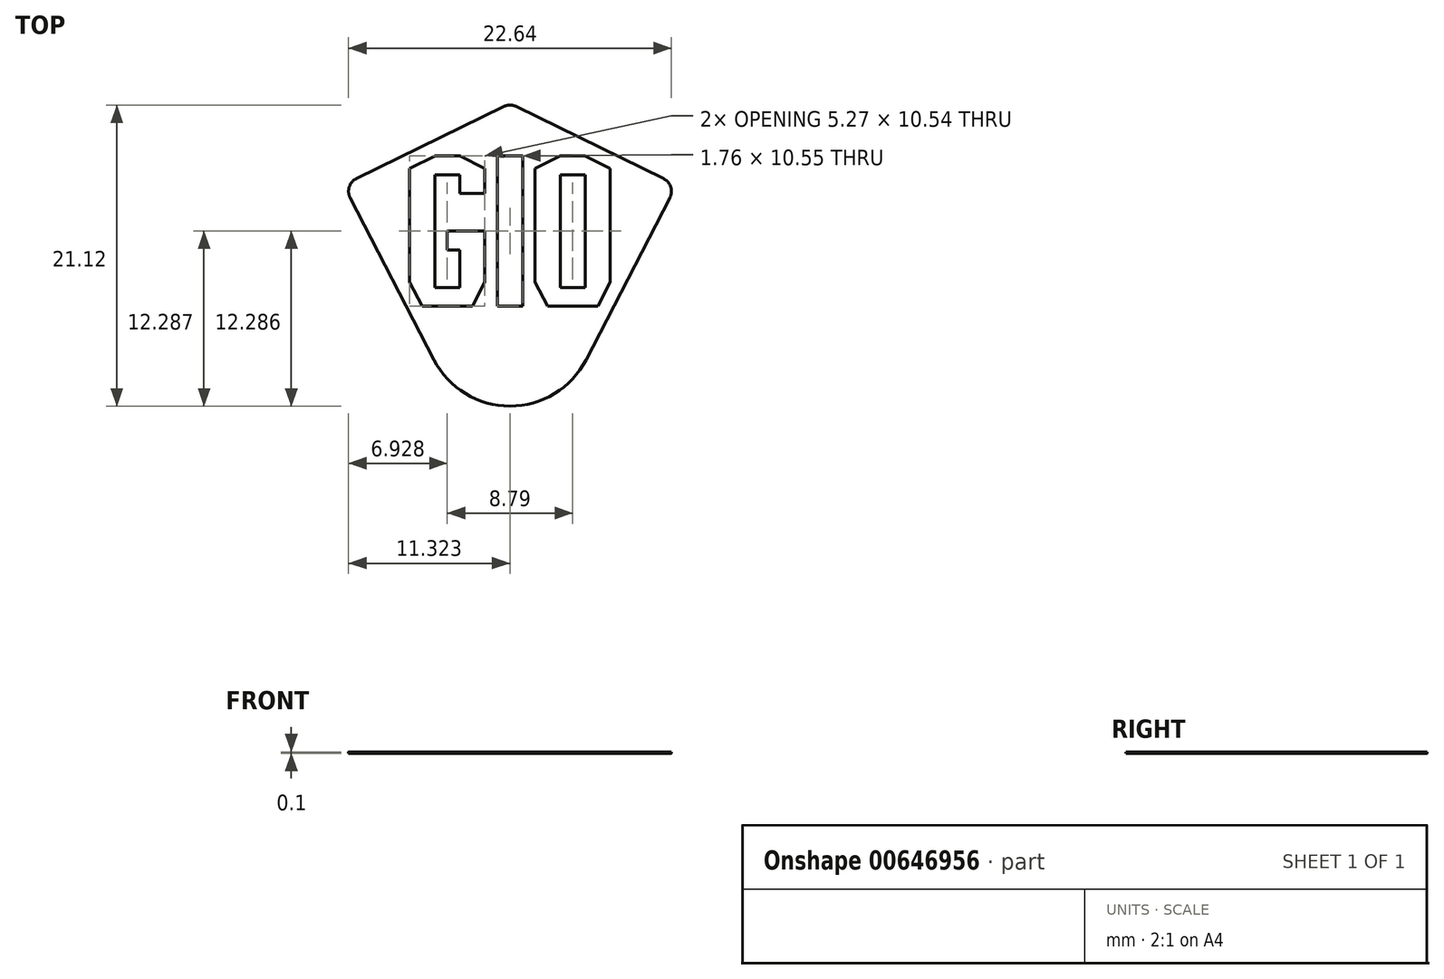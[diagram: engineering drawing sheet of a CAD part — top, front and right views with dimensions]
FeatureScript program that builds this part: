
annotation { "Feature Type Name" : "Feature", "Feature Type Description" : "" }
export const myFeature = defineFeature(function(context is Context, id is Id, definition is map)
    precondition{}
    {
        {
            var Q0;
            Q0=qCreatedBy(makeId("Top.planeOp"),FACE);
            var sketch = newSketch(context, id + "F0", { "sketchPlane" : qUnion([Q0])});
            skArc(sketch, "E0.MirrorCS", {"start": v(-12.62, 8.93) * mm, "mid": v(-12.18, 9.03) * mm, "end": v(-11.74, 8.93) * mm});
            skArc(sketch, "E1.MirrorCS", {"start": v(-1.42, 3.88) * mm, "mid": v(-0.9, 3.3) * mm, "end": v(-0.97, 2.52) * mm});
            skArc(sketch, "E2.MirrorCS", {"start": v(-23.38, 2.52) * mm, "mid": v(-23.45, 3.3) * mm, "end": v(-22.94, 3.88) * mm});
            skPoint(sketch, "E3.MirrorP", {"position": v(-23.85, 3.43) * mm});
            skArc(sketch, "E4.MirrorCS", {"start": v(-6.85, -8.84) * mm, "mid": v(-12.18, -12.09) * mm, "end": v(-17.5, -8.84) * mm});
            skLineSegment(sketch, "E5.MirrorCS", {"start": v(-6.85, -8.84) * mm, "end": v(-0.97, 2.52) * mm});
            skLineSegment(sketch, "E6.MirrorCS", {"start": v(-12.62, 8.93) * mm, "end": v(-22.94, 3.88) * mm});
            skLineSegment(sketch, "E7.MirrorCS", {"start": v(-23.38, 2.52) * mm, "end": v(-17.5, -8.84) * mm});
            skLineSegment(sketch, "E8.MirrorCS", {"start": v(-1.42, 3.88) * mm, "end": v(-11.74, 8.93) * mm});
            skLineSegment(sketch, "E9", {"start": v(-22.26, 2.53) * mm, "end": v(-16.62, -8.38) * mm});
            skArc(sketch, "E10.filletArc", {"start": v(-9.67, -10.41) * mm, "mid": v(-8.56, -9.53) * mm, "end": v(-7.74, -8.38) * mm});
            skPoint(sketch, "E11", {"position": v(-16.57, -8.47) * mm});
            skPoint(sketch, "E12", {"position": v(-15.25, -10.03) * mm});
            skPoint(sketch, "E13", {"position": v(-13.94, -10.77) * mm});
            skPoint(sketch, "E14", {"position": v(-13.06, -11) * mm});
            skPoint(sketch, "E15", {"position": v(-11.3, -11) * mm});
            skPoint(sketch, "E16", {"position": v(-10.42, -10.77) * mm});
            skPoint(sketch, "E17", {"position": v(-9.1, -10.03) * mm});
            skPoint(sketch, "E18", {"position": v(-9.1, -6.67) * mm});
            skPoint(sketch, "E19", {"position": v(-2.78, 1.2) * mm});
            skPoint(sketch, "E20", {"position": v(-9.1, 6.52) * mm});
            skPoint(sketch, "E21", {"position": v(-10.42, 7.17) * mm});
            skPoint(sketch, "E22", {"position": v(-11.3, 7.6) * mm});
            skPoint(sketch, "E23", {"position": v(-13.06, 7.6) * mm});
            skPoint(sketch, "E24", {"position": v(-13.94, 7.17) * mm});
            skPoint(sketch, "E25", {"position": v(-13.06, 5.37) * mm});
            skPoint(sketch, "E26", {"position": v(-10.42, 4.94) * mm});
            skPoint(sketch, "E27", {"position": v(-11.3, 5.37) * mm});
            skPoint(sketch, "E28", {"position": v(-21.58, 1.2) * mm});
            skLineSegment(sketch, "E29", {"start": v(-7.74, -8.38) * mm, "end": v(-2.78, 1.2) * mm});
            skLineSegment(sketch, "E30", {"start": v(-2.78, 1.2) * mm, "end": v(-2.1, 2.53) * mm});
            skLineSegment(sketch, "E31", {"start": v(-2.32, 3.2) * mm, "end": v(-9.1, 6.52) * mm});
            skLineSegment(sketch, "E32", {"start": v(-22.04, 3.2) * mm, "end": v(-14.65, 6.82) * mm});
            skLineSegment(sketch, "E33", {"start": v(-12.78, 7.74) * mm, "end": v(-12.4, 7.92) * mm});
            skLineSegment(sketch, "E34", {"start": v(-11.96, 7.92) * mm, "end": v(-11.58, 7.74) * mm});
            skLineSegment(sketch, "E35", {"start": v(-9.1, 6.52) * mm, "end": v(-9.7, 6.82) * mm});
            skArc(sketch, "E36.filletArc", {"start": v(-22.04, 3.2) * mm, "mid": v(-22.3, 2.91) * mm, "end": v(-22.26, 2.53) * mm});
            skArc(sketch, "E37.filletArc", {"start": v(-2.1, 2.53) * mm, "mid": v(-2.06, 2.91) * mm, "end": v(-2.32, 3.2) * mm});
            skArc(sketch, "E38.filletArc", {"start": v(-13.94, 6.37) * mm, "mid": v(-14.17, 6.8) * mm, "end": v(-14.65, 6.82) * mm});
            skArc(sketch, "E39.filletArc", {"start": v(-9.7, 6.82) * mm, "mid": v(-10.18, 6.8) * mm, "end": v(-10.42, 6.37) * mm});
            skLineSegment(sketch, "E40", {"start": v(-13.94, 4.14) * mm, "end": v(-13.94, 6.37) * mm});
            skArc(sketch, "E41.filletArc", {"start": v(-11.96, 7.92) * mm, "mid": v(-12.18, 7.97) * mm, "end": v(-12.4, 7.92) * mm});
            skArc(sketch, "E42.filletArc", {"start": v(-12.78, 7.74) * mm, "mid": v(-12.98, 7.55) * mm, "end": v(-13.06, 7.29) * mm});
            skArc(sketch, "E43.filletArc", {"start": v(-11.3, 7.29) * mm, "mid": v(-11.37, 7.55) * mm, "end": v(-11.58, 7.74) * mm});
            skArc(sketch, "E44.filletArc", {"start": v(-10.42, -9.98) * mm, "mid": v(-10.17, -10.41) * mm, "end": v(-9.67, -10.41) * mm});
            skArc(sketch, "E45.MirrorCS", {"start": v(-14.69, -10.41) * mm, "mid": v(-15.8, -9.53) * mm, "end": v(-16.62, -8.38) * mm});
            skArc(sketch, "E46.MirrorCS", {"start": v(-13.94, -9.98) * mm, "mid": v(-14.19, -10.41) * mm, "end": v(-14.69, -10.41) * mm});
            skArc(sketch, "E47", {"start": v(-12.63, -11.1) * mm, "mid": v(-12.18, -11.14) * mm, "end": v(-11.72, -11.1) * mm});
            skLineSegment(sketch, "E48", {"start": v(-13.94, -9.98) * mm, "end": v(-13.94, -0.3) * mm});
            skLineSegment(sketch, "E49", {"start": v(-13.06, -10.61) * mm, "end": v(-13.06, 7.29) * mm});
            skLineSegment(sketch, "E50", {"start": v(-11.3, 7.29) * mm, "end": v(-11.3, -10.61) * mm});
            skArc(sketch, "E51.filletArc", {"start": v(-13.06, -10.61) * mm, "mid": v(-12.94, -10.94) * mm, "end": v(-12.63, -11.1) * mm});
            skArc(sketch, "E52.filletArc", {"start": v(-11.72, -11.1) * mm, "mid": v(-11.42, -10.94) * mm, "end": v(-11.3, -10.61) * mm});
            skLineSegment(sketch, "E53", {"start": v(-12.18, 8.03) * mm, "end": v(-12.18, -6.09) * mm});
            skLineSegment(sketch, "E54.MirrorCS", {"start": v(-10.42, 8.03) * mm, "end": v(-10.42, -6.09) * mm});
            skLineSegment(sketch, "E55", {"start": v(-10.42, -6.09) * mm, "end": v(-10.42, -16.87) * mm});
            skPoint(sketch, "E56.endSnap0", {"position": v(-8.56, -9.53) * mm});
            skPoint(sketch, "E57", {"position": v(-10.42, 4.15) * mm});
            skPoint(sketch, "E58", {"position": v(-8.66, 5.47) * mm});
            skPoint(sketch, "E59", {"position": v(-6.9, 5.47) * mm});
            skPoint(sketch, "E60", {"position": v(-5.15, 4.59) * mm});
            skPoint(sketch, "E61", {"position": v(-13.06, 5.47) * mm});
            skPoint(sketch, "E62", {"position": v(-11.3, 5.47) * mm});
            skPoint(sketch, "E63", {"position": v(-6.9, 4.15) * mm});
            skLineSegment(sketch, "E64", {"start": v(-8.66, 5.47) * mm, "end": v(-6.9, 5.47) * mm});
            skPoint(sketch, "E65", {"position": v(-5.15, -3.38) * mm});
            skPoint(sketch, "E66", {"position": v(-6.02, -5.07) * mm});
            skLineSegment(sketch, "E67", {"start": v(-5.15, 4.59) * mm, "end": v(-5.15, -3.38) * mm});
            skPoint(sketch, "E68", {"position": v(-6.7, -6.4) * mm});
            skPoint(sketch, "E69.MirrorP", {"position": v(-9.54, -5.07) * mm});
            skPoint(sketch, "E70.MirrorP", {"position": v(-8.86, -6.4) * mm});
            skLineSegment(sketch, "E71.MirrorCS", {"start": v(-10.42, 4.59) * mm, "end": v(-10.42, -3.38) * mm});
            skPoint(sketch, "E72.MirrorP", {"position": v(-10.42, 4.59) * mm});
            skPoint(sketch, "E73.MirrorP", {"position": v(-10.42, -3.38) * mm});
            skLineSegment(sketch, "E74", {"start": v(-10.42, -3.38) * mm, "end": v(-9.54, -5.07) * mm});
            skLineSegment(sketch, "E75", {"start": v(-10.42, -3.38) * mm, "end": v(-10.42, 4.15) * mm});
            skPoint(sketch, "E76", {"position": v(-6.9, -3.76) * mm});
            skPoint(sketch, "E77", {"position": v(-8.66, -3.76) * mm});
            skPoint(sketch, "E78", {"position": v(-8.66, 4.15) * mm});
            skLineSegment(sketch, "E79", {"start": v(-10.42, 4.15) * mm, "end": v(-10.42, -3.38) * mm});
            skLineSegment(sketch, "E80", {"start": v(-8.66, -3.76) * mm, "end": v(-8.66, 4.15) * mm});
            skLineSegment(sketch, "E81", {"start": v(-6.9, 4.15) * mm, "end": v(-6.9, -3.76) * mm});
            skLineSegment(sketch, "E82", {"start": v(-8.66, 4.15) * mm, "end": v(-6.9, 4.15) * mm});
            skLineSegment(sketch, "E83", {"start": v(-8.66, -3.76) * mm, "end": v(-6.9, -3.76) * mm});
            skPoint(sketch, "E84", {"position": v(-11.3, -5.08) * mm});
            skPoint(sketch, "E85", {"position": v(-13.06, -5.08) * mm});
            skLineSegment(sketch, "E86", {"start": v(-13.06, -5.08) * mm, "end": v(-11.3, -5.08) * mm});
            skLineSegment(sketch, "E87", {"start": v(-13.06, 5.47) * mm, "end": v(-11.3, 5.47) * mm});
            skPoint(sketch, "E88", {"position": v(-7.78, 4.15) * mm});
            skPoint(sketch, "E89", {"position": v(-7.78, -3.76) * mm});
            skLineSegment(sketch, "E90", {"start": v(-7.78, 4.15) * mm, "end": v(-7.78, -3.76) * mm});
            skLineSegment(sketch, "E91", {"start": v(-10.42, 4.59) * mm, "end": v(-8.66, 5.47) * mm});
            skLineSegment(sketch, "E92.MirrorCS", {"start": v(-17.45, 4.15) * mm, "end": v(-17.45, -3.76) * mm});
            skLineSegment(sketch, "E93.MirrorCS", {"start": v(-15.7, 4.15) * mm, "end": v(-17.45, 4.15) * mm});
            skLineSegment(sketch, "E94.MirrorCS", {"start": v(-15.7, -3.76) * mm, "end": v(-17.45, -3.76) * mm});
            skLineSegment(sketch, "E95.MirrorCS", {"start": v(-19.2, 4.59) * mm, "end": v(-19.2, -3.38) * mm});
            skLineSegment(sketch, "E96.MirrorCS", {"start": v(-15.7, 5.47) * mm, "end": v(-17.45, 5.47) * mm});
            skLineSegment(sketch, "E97.MirrorCS", {"start": v(-13.94, 4.59) * mm, "end": v(-15.7, 5.47) * mm});
            skLineSegment(sketch, "E98.MirrorCS", {"start": v(-13.94, 4.59) * mm, "end": v(-13.94, -3.38) * mm});
            skLineSegment(sketch, "E99.MirrorCS", {"start": v(-13.94, -3.38) * mm, "end": v(-14.81, -5.07) * mm});
            skLineSegment(sketch, "E100", {"start": v(-15.7, 2.83) * mm, "end": v(-13.94, 2.83) * mm});
            skPoint(sketch, "E101", {"position": v(-15.7, 1.51) * mm});
            skPoint(sketch, "E102", {"position": v(-17.45, 1.51) * mm});
            skPoint(sketch, "E103", {"position": v(-16.57, 1.51) * mm});
            skLineSegment(sketch, "E104", {"start": v(-15.7, 2.83) * mm, "end": v(-15.7, 4.15) * mm});
            skLineSegment(sketch, "E105", {"start": v(-16.57, 0.2) * mm, "end": v(-15.7, 0.2) * mm});
            skLineSegment(sketch, "E106.MirrorCS", {"start": v(-15.7, -1.12) * mm, "end": v(-16.57, -1.12) * mm});
            skLineSegment(sketch, "E107", {"start": v(-15.7, 0.2) * mm, "end": v(-13.94, 0.2) * mm});
            skLineSegment(sketch, "E108", {"start": v(-16.57, 0.2) * mm, "end": v(-16.57, -1.12) * mm});
            skLineSegment(sketch, "E109", {"start": v(-15.7, -3.76) * mm, "end": v(-15.7, -1.12) * mm});
            skLineSegment(sketch, "E110", {"start": v(-9.54, -5.07) * mm, "end": v(-6.02, -5.07) * mm});
            skLineSegment(sketch, "E111.MirrorCS", {"start": v(-14.81, -5.07) * mm, "end": v(-18.33, -5.07) * mm});
            skSolve(sketch);
        }
        {
            var Q0;
            Q0=makeQuery(id+"F0.imprint","IMPRINT",FACE,{"disambiguationData":[TD([[makeQuery(id+"F0.imprint","IMPRINT",EDGE,{"derivedFrom":sQuery(id+"F0.wireOp",EDGE,"E0.MirrorCS")}),-1.0]])]});
            var Q1;
            {var subQ5=sQuery(id+"F0.wireOp",EDGE,"E2.MirrorCS");Q1=makeQuery(id+"F0.imprint","IMPRINT",FACE,{"disambiguationData":[TD([[makeQuery(id+"F0.imprint","IMPRINT",EDGE,{"derivedFrom":subQ5}),-1.0]])]});}
            var Q2;
            {var subQ7=sQuery(id+"F0.wireOp",EDGE,"E4.MirrorCS");Q2=makeQuery(id+"F0.imprint","IMPRINT",FACE,{"disambiguationData":[TD([[makeQuery(id+"F0.imprint","IMPRINT",EDGE,{"derivedFrom":subQ7}),-1.0]])]});}
            var Q3;
            Q3=makeQuery(id+"F0.imprint","IMPRINT",FACE,{"disambiguationData":[TD([[makeQuery(id+"F0.imprint","IMPRINT",EDGE,{"derivedFrom":sQuery(id+"F0.wireOp",EDGE,"i4NC8C4y-CYhM-9ifA-fVI3-dGYLjBYDZOpJ.bottom")}),-1.0]])]});
            var Q4;
            {var subQ0=sQuery(id+"F0.wireOp",EDGE,"54byzUAP-60Q0-1v49-qkVZ-HTfB0HKNuxzY");var subQ1=sQuery(id+"F0.wireOp",EDGE,"d3f79946-6490-41ce-9ba5-b02d18e1b7880.MirrorCS");var subQ2=makeQuery(id+"F0.imprint","INTERSECT",VERTEX,{"derivedFrom":[subQ1,subQ0]});Q4=makeQuery(id+"F0.imprint","IMPRINT",FACE,{"disambiguationData":[TD([[makeQuery(id+"F0.imprint","IMPRINT",EDGE,{"disambiguationData":[TD([[subQ2,-1.0]])],"derivedFrom":subQ1}),-1.0]])]});}
            var Q5;
            {var subQ1=sQuery(id+"F0.wireOp",EDGE,"d3f79946-6490-41ce-9ba5-b02d18e1b7880.MirrorCS");var subQ7=makeQuery(id+"F0.imprint","INTERSECT",VERTEX,{"derivedFrom":[subQ1,sQuery(id+"F0.wireOp",EDGE,"b1231559-5cb8-4e33-ac14-762cc1e6672f0.MirrorCS")]});Q5=makeQuery(id+"F0.imprint","IMPRINT",FACE,{"disambiguationData":[TD([[makeQuery(id+"F0.imprint","IMPRINT",EDGE,{"disambiguationData":[TD([[subQ7,1.0]])],"derivedFrom":subQ1}),-1.0]])]});}
            var Q6;
            {var subQ13=sQuery(id+"F0.wireOp",EDGE,"E1.MirrorCS");Q6=makeQuery(id+"F0.imprint","IMPRINT",FACE,{"disambiguationData":[TD([[makeQuery(id+"F0.imprint","IMPRINT",EDGE,{"derivedFrom":subQ13}),-1.0]])]});}
            var Q7;
            {var subQ0=sQuery(id+"F0.wireOp",EDGE,"54byzUAP-60Q0-1v49-qkVZ-HTfB0HKNuxzY");var subQ1=sQuery(id+"F0.wireOp",EDGE,"E8.MirrorCS");var subQ2=makeQuery(id+"F0.imprint","INTERSECT",VERTEX,{"derivedFrom":[subQ1,subQ0]});Q7=makeQuery(id+"F0.imprint","IMPRINT",FACE,{"disambiguationData":[TD([[makeQuery(id+"F0.imprint","IMPRINT",EDGE,{"disambiguationData":[TD([[subQ2,-1.0]])],"derivedFrom":subQ1}),1.0]])]});}
            var Q8;
            {var subQ0=sQuery(id+"F0.wireOp",EDGE,"b1231559-5cb8-4e33-ac14-762cc1e6672f0.MirrorCS");var subQ1=sQuery(id+"F0.wireOp",EDGE,"E5.MirrorCS");var subQ2=makeQuery(id+"F0.imprint","INTERSECT",VERTEX,{"derivedFrom":[subQ1,subQ0]});Q8=makeQuery(id+"F0.imprint","IMPRINT",FACE,{"disambiguationData":[TD([[makeQuery(id+"F0.imprint","IMPRINT",EDGE,{"disambiguationData":[TD([[subQ2,-1.0]])],"derivedFrom":subQ1}),1.0]])]});}
            var Q9;
            {var subQ0=sQuery(id+"F0.wireOp",EDGE,"x39NxPae-PUvZ-Uhhi-99mf-Z52wYtiFz4lC");var subQ1=sQuery(id+"F0.wireOp",EDGE,"E5.MirrorCS");var subQ2=makeQuery(id+"F0.imprint","INTERSECT",VERTEX,{"derivedFrom":[subQ1,subQ0]});Q9=makeQuery(id+"F0.imprint","IMPRINT",FACE,{"disambiguationData":[TD([[makeQuery(id+"F0.imprint","IMPRINT",EDGE,{"disambiguationData":[TD([[subQ2,-1.0]])],"derivedFrom":subQ1}),1.0]])]});}
            var Q10;
            {var subQ5=sQuery(id+"F0.wireOp",EDGE,"U7k8mDXT-bmFV-EHft-UU3T-YDVJH7ch8q10");var subQ10=sQuery(id+"F0.wireOp",EDGE,"b1231559-5cb8-4e33-ac14-762cc1e6672f0.MirrorCS");var subQ12=makeQuery(id+"F0.imprint","INTERSECT",VERTEX,{"derivedFrom":[subQ5,subQ10]});Q10=makeQuery(id+"F0.imprint","IMPRINT",FACE,{"disambiguationData":[TD([[makeQuery(id+"F0.imprint","IMPRINT",EDGE,{"disambiguationData":[TD([[subQ12,-1.0]])],"derivedFrom":subQ5}),1.0]])]});}
            var Q11;
            {var subQ0=sQuery(id+"F0.wireOp",EDGE,"E38.filletArc");Q11=makeQuery(id+"F0.imprint","IMPRINT",FACE,{"disambiguationData":[TD([[makeQuery(id+"F0.imprint","IMPRINT",EDGE,{"derivedFrom":subQ0}),1.0]])]});}
            var Q12;
            Q12=makeQuery(id+"F0.imprint","IMPRINT",FACE,{"disambiguationData":[TD([[makeQuery(id+"F0.imprint","IMPRINT",EDGE,{"derivedFrom":sQuery(id+"F0.wireOp",EDGE,"E33")}),-1.0]])]});
            var Q13;
            {var subQ1=sQuery(id+"F0.wireOp",EDGE,"E35");Q13=makeQuery(id+"F0.imprint","IMPRINT",FACE,{"disambiguationData":[TD([[makeQuery(id+"F0.imprint","IMPRINT",EDGE,{"derivedFrom":subQ1}),1.0]])]});}
            var Q14;
            {var subQ0=sQuery(id+"F0.wireOp",EDGE,"E46.MirrorCS");Q14=makeQuery(id+"F0.imprint","IMPRINT",FACE,{"disambiguationData":[TD([[makeQuery(id+"F0.imprint","IMPRINT",EDGE,{"derivedFrom":subQ0}),-1.0]])]});}
            var Q15;
            {var subQ0=sQuery(id+"F0.wireOp",EDGE,"E45.MirrorCS");var subQ1=sQuery(id+"F0.wireOp",EDGE,"E9");var subQ2=makeQuery(id+"F0.imprint","INTERSECT",VERTEX,{"derivedFrom":[subQ1,subQ0]});Q15=makeQuery(id+"F0.imprint","IMPRINT",FACE,{"disambiguationData":[TD([[makeQuery(id+"F0.imprint","IMPRINT",EDGE,{"disambiguationData":[TD([[subQ2,1.0]])],"derivedFrom":subQ1}),1.0]])]});}
            var Q16;
            Q16=makeQuery(id+"F0.imprint","IMPRINT",FACE,{"disambiguationData":[TD([[makeQuery(id+"F0.imprint","IMPRINT",EDGE,{"derivedFrom":sQuery(id+"F0.wireOp",EDGE,"E47")}),1.0]])]});
            var Q17;
            {var subQ2=sQuery(id+"F0.wireOp",EDGE,"E10.filletArc");Q17=makeQuery(id+"F0.imprint","IMPRINT",FACE,{"disambiguationData":[TD([[makeQuery(id+"F0.imprint","IMPRINT",EDGE,{"derivedFrom":subQ2}),1.0]])]});}
            var Q18;
            {var subQ0=sQuery(id+"F0.wireOp",EDGE,"54byzUAP-60Q0-1v49-qkVZ-HTfB0HKNuxzY");var subQ1=sQuery(id+"F0.wireOp",EDGE,"E31");var subQ2=makeQuery(id+"F0.imprint","INTERSECT",VERTEX,{"derivedFrom":[subQ1,subQ0]});Q18=makeQuery(id+"F0.imprint","IMPRINT",FACE,{"disambiguationData":[TD([[makeQuery(id+"F0.imprint","IMPRINT",EDGE,{"disambiguationData":[TD([[subQ2,-1.0]])],"derivedFrom":subQ1}),1.0]])]});}
            var Q19;
            {var subQ4=sQuery(id+"F0.wireOp",EDGE,"E30");Q19=makeQuery(id+"F0.imprint","IMPRINT",FACE,{"disambiguationData":[TD([[makeQuery(id+"F0.imprint","IMPRINT",EDGE,{"derivedFrom":subQ4}),1.0]])]});}
            var Q20;
            Q20=makeQuery(id+"F0.imprint","IMPRINT",FACE,{"disambiguationData":[TD([[makeQuery(id+"F0.imprint","IMPRINT",EDGE,{"derivedFrom":sQuery(id+"F0.wireOp",EDGE,"E92.MirrorCS")}),1.0]])]});
            var Q21;
            {var subQ0=sQuery(id+"F0.wireOp",EDGE,"E36.filletArc");Q21=makeQuery(id+"F0.imprint","IMPRINT",FACE,{"disambiguationData":[TD([[makeQuery(id+"F0.imprint","IMPRINT",EDGE,{"derivedFrom":subQ0}),1.0]])]});}
            var Q22;
            {var subQ5=sQuery(id+"F0.wireOp",EDGE,"E34");Q22=makeQuery(id+"F0.imprint","IMPRINT",FACE,{"disambiguationData":[TD([[makeQuery(id+"F0.imprint","IMPRINT",EDGE,{"derivedFrom":subQ5}),-1.0]])]});}
            var Q23;
            {var subQ0=sQuery(id+"F0.wireOp",EDGE,"E80");Q23=makeQuery(id+"F0.imprint","IMPRINT",FACE,{"disambiguationData":[TD([[makeQuery(id+"F0.imprint","IMPRINT",EDGE,{"derivedFrom":subQ0}),-1.0]])]});}
            var Q24;
            {var subQ0=sQuery(id+"F0.wireOp",EDGE,"E81");Q24=makeQuery(id+"F0.imprint","IMPRINT",FACE,{"disambiguationData":[TD([[makeQuery(id+"F0.imprint","IMPRINT",EDGE,{"derivedFrom":subQ0}),-1.0]])]});}
            extrude(context, id + "F1", {"entities" : qUnion([Q0, Q1, Q2, Q3, Q4, Q5, Q6, Q7, Q8, Q9, Q10, Q11, Q12, Q13, Q14, Q15, Q16, Q17, Q18, Q19, Q20, Q21, Q22, Q23, Q24]), "depth" : .1 * mm, "offsetDistance" : 25 * mm});
        }
    });
